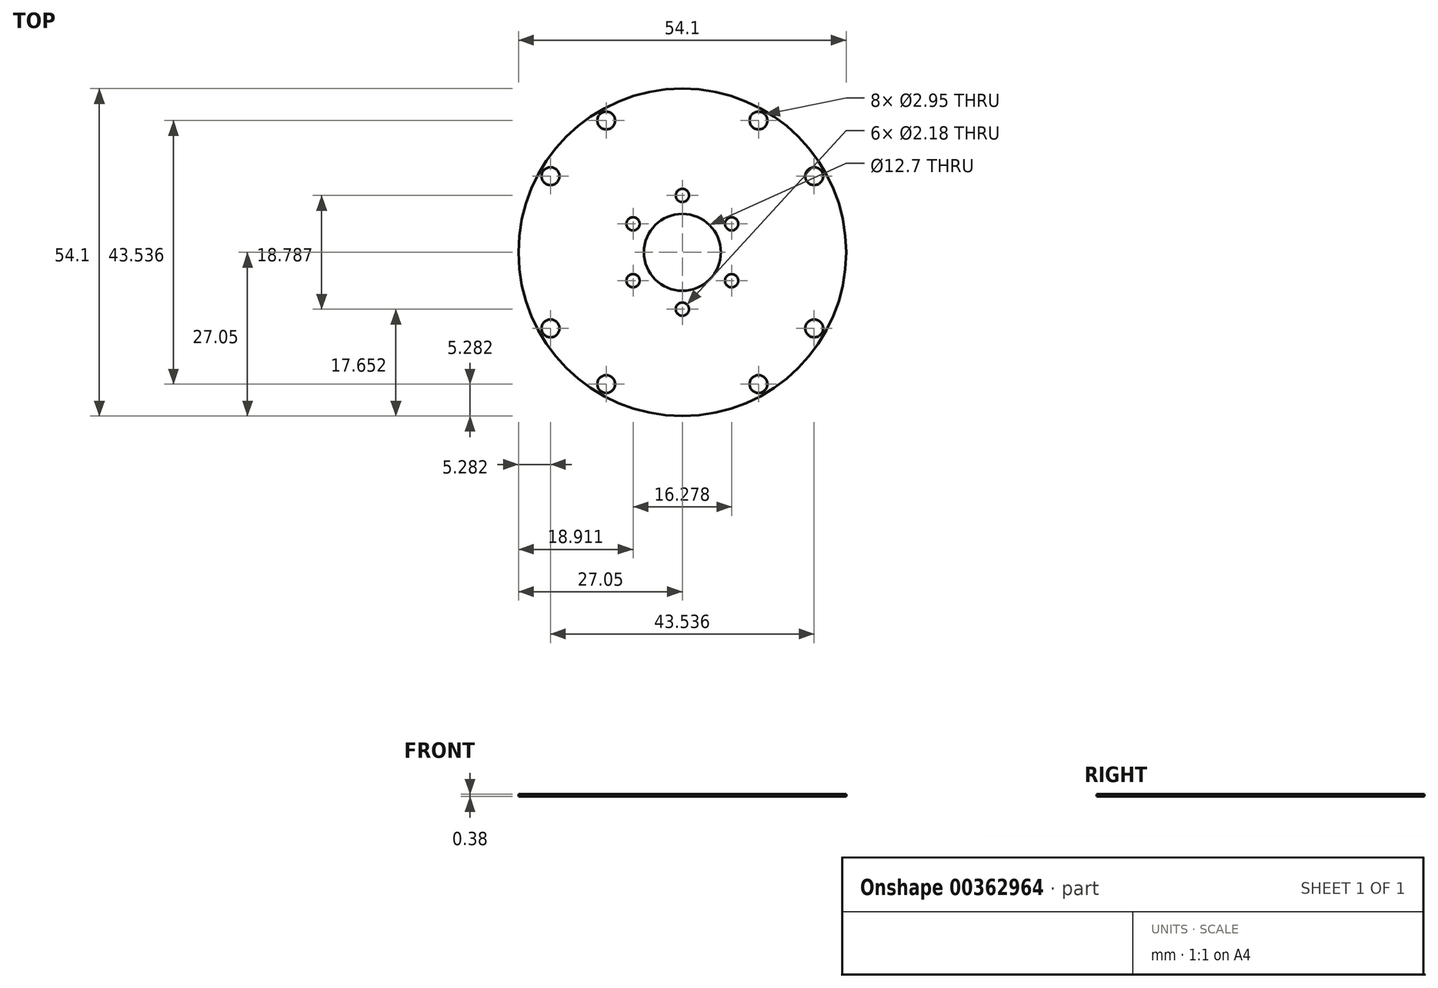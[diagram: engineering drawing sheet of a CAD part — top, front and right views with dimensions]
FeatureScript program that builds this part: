
annotation { "Feature Type Name" : "Feature", "Feature Type Description" : "" }
export const myFeature = defineFeature(function(context is Context, id is Id, definition is map)
    precondition{}
    {
        {
            var Q0;
            Q0=qCreatedBy(makeId("Top.planeOp"),FACE);
            var sketch = newSketch(context, id + "F0", { "sketchPlane" : qUnion([Q0])});
            skCircle(sketch, "E0", {"center": v(0, 0) * mm, "radius": 27.05 * mm});
            skCircle(sketch, "E1", {"center": v(0, 0) * mm, "radius": 6.35 * mm});
            skPoint(sketch, "E2", {"position": v(12.57, 21.77) * mm});
            skPoint(sketch, "E3", {"position": v(21.77, 12.57) * mm});
            skPoint(sketch, "E4", {"position": v(0, -9.4) * mm});
            skPoint(sketch, "E5", {"position": v(8.13, -4.7) * mm});
            skPoint(sketch, "E6.1.0", {"position": v(-21.77, 12.57) * mm});
            skPoint(sketch, "E6.1.1", {"position": v(-12.57, 21.77) * mm});
            skPoint(sketch, "E6.2.0", {"position": v(-12.57, -21.77) * mm});
            skPoint(sketch, "E6.2.1", {"position": v(-21.77, -12.57) * mm});
            skPoint(sketch, "E6.3.0", {"position": v(21.77, -12.57) * mm});
            skPoint(sketch, "E6.3.1", {"position": v(12.57, -21.77) * mm});
            skPoint(sketch, "E7.1.0", {"position": v(0, 9.39) * mm});
            skPoint(sketch, "E7.1.1", {"position": v(8.14, 4.7) * mm});
            skPoint(sketch, "E7.2.0", {"position": v(-8.13, -4.69) * mm});
            skPoint(sketch, "E7.2.1", {"position": v(-8.14, 4.7) * mm});
            skSolve(sketch);
        }
        {
            var Q0;
            Q0=makeQuery(id+"F0.imprint","IMPRINT",FACE,{"disambiguationData":[TD([[makeQuery(id+"F0.imprint","IMPRINT",EDGE,{"derivedFrom":sQuery(id+"F0.wireOp",EDGE,"E0")}),1.0]])]});
            extrude(context, id + "F1", {"entities" : qUnion([Q0]), "depth" : 0.38 * mm});
        }
        {
            var Q0;
            Q0=sQuery(id+"F0.wireOp",VERTEX,"E6.1.0");
            var Q1;
            Q1=sQuery(id+"F0.wireOp",VERTEX,"E6.1.1");
            var Q2;
            Q2=sQuery(id+"F0.wireOp",VERTEX,"E2");
            var Q3;
            Q3=sQuery(id+"F0.wireOp",VERTEX,"E3");
            var Q4;
            Q4=sQuery(id+"F0.wireOp",VERTEX,"E6.3.0");
            var Q5;
            Q5=sQuery(id+"F0.wireOp",VERTEX,"E6.3.1");
            var Q6;
            Q6=sQuery(id+"F0.wireOp",VERTEX,"E6.2.0");
            var Q7;
            Q7=sQuery(id+"F0.wireOp",VERTEX,"E6.2.1");
            var Q8;
            Q8=makeQuery(id+"F1.opExtrude","SWEPT_BODY",BODY,{"disambiguationData":[OSD([sQuery(id+"F0.wireOp",EDGE,"E0"),sQuery(id+"F0.wireOp",EDGE,"E1")])]});
            hole(context, id + "F2", {"style" : HoleStyle.SIMPLE, "endStyle" : HoleEndStyle.THROUGH, "oppositeDirection" : true, "standardTappedOrClearance" : lookupTablePath({ "standard" : "ANSI", "size" : "#32 (0.12)", "type" : "Drilled" }), "standardBlindInLast" : lookupTablePath({ "standard" : "ANSI", "size" : "#32", "type" : "Drilled" }), "holeDiameter" : 2.95 * mm, "isTappedThrough" : true, "tappedDepth" : 4.57 * mm, "tapClearance" : 3, "startFromSketch" : true, "locations" : qUnion([Q0, Q1, Q2, Q3, Q4, Q5, Q6, Q7]), "scope" : qUnion([Q8])});
        }
        {
            var Q0;
            Q0=sQuery(id+"F0.wireOp",VERTEX,"E4");
            var Q1;
            Q1=sQuery(id+"F0.wireOp",VERTEX,"E5");
            var Q2;
            Q2=sQuery(id+"F0.wireOp",VERTEX,"E7.2.1");
            var Q3;
            Q3=sQuery(id+"F0.wireOp",VERTEX,"E0.center");
            var Q4;
            Q4=sQuery(id+"F0.wireOp",VERTEX,"E7.1.0");
            var Q5;
            Q5=sQuery(id+"F0.wireOp",VERTEX,"E7.1.1");
            var Q6;
            Q6=sQuery(id+"F0.wireOp",VERTEX,"E7.2.0");
            var Q7;
            Q7=makeQuery(id+"F1.opExtrude","SWEPT_BODY",BODY,{"disambiguationData":[OSD([sQuery(id+"F0.wireOp",EDGE,"E0"),sQuery(id+"F0.wireOp",EDGE,"E1")])]});
            hole(context, id + "F3", {"style" : HoleStyle.SIMPLE, "endStyle" : HoleEndStyle.THROUGH, "oppositeDirection" : true, "standardTappedOrClearance" : lookupTablePath({ "standard" : "ANSI", "size" : "#44 (0.09)", "type" : "Drilled" }), "standardBlindInLast" : lookupTablePath({ "standard" : "ANSI", "size" : "#44", "type" : "Drilled" }), "holeDiameter" : 2.18 * mm, "isTappedThrough" : true, "tappedDepth" : 4.57 * mm, "tapClearance" : 3, "startFromSketch" : true, "locations" : qUnion([Q0, Q1, Q2, Q3, Q4, Q5, Q6]), "scope" : qUnion([Q7])});
        }
    });
